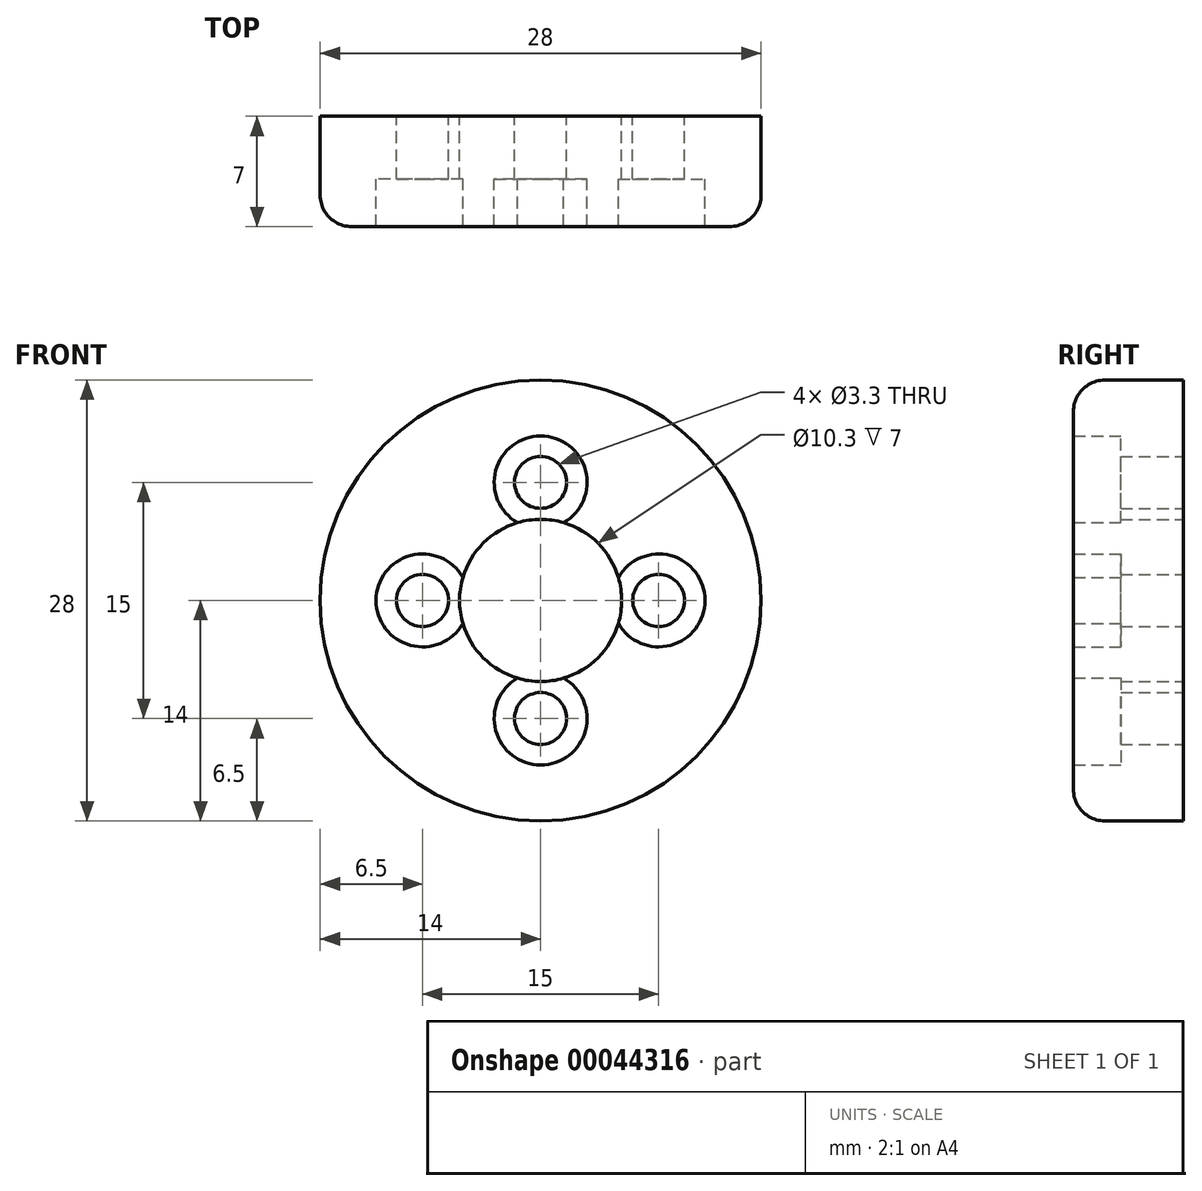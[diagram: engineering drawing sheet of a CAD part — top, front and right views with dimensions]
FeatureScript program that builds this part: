
annotation { "Feature Type Name" : "Feature", "Feature Type Description" : "" }
export const myFeature = defineFeature(function(context is Context, id is Id, definition is map)
    precondition{}
    {
        {
            var Q0;
            Q0=qCreatedBy(makeId("Front.planeOp"),FACE);
            var sketch = newSketch(context, id + "F0", { "sketchPlane" : qUnion([Q0])});
            skCircle(sketch, "E0", {"center": v(0, 0) * mm, "radius": 14 * mm});
            skCircle(sketch, "E1", {"center": v(0, 0) * mm, "radius": 5.15 * mm});
            skCircle(sketch, "E2", {"center": v(0, 0) * mm, "radius": 7.5 * mm, "construction": true});
            skLineSegment(sketch, "E3", {"start": v(0, 0) * mm, "end": v(0, 7.5) * mm});
            skCircle(sketch, "E4", {"center": v(0, 7.5) * mm, "radius": 1.65 * mm});
            skCircle(sketch, "E5.1.0", {"center": v(-7.5, 0) * mm, "radius": 1.65 * mm});
            skCircle(sketch, "E5.2.0", {"center": v(0, -7.5) * mm, "radius": 1.65 * mm});
            skCircle(sketch, "E5.3.0", {"center": v(7.5, 0) * mm, "radius": 1.65 * mm});
            skCircle(sketch, "E6", {"center": v(0, 7.5) * mm, "radius": 2.95 * mm});
            skCircle(sketch, "E7.1.0", {"center": v(-7.5, 0) * mm, "radius": 2.95 * mm});
            skCircle(sketch, "E7.2.0", {"center": v(0, -7.5) * mm, "radius": 2.95 * mm});
            skCircle(sketch, "E7.3.0", {"center": v(7.5, 0) * mm, "radius": 2.95 * mm});
            skSolve(sketch);
        }
        {
            var Q0;
            Q0=makeQuery(id+"F0.imprint","IMPRINT",FACE,{"disambiguationData":[TD([[makeQuery(id+"F0.imprint","IMPRINT",EDGE,{"derivedFrom":sQuery(id+"F0.wireOp",EDGE,"E0")}),1.0]])]});
            extrude(context, id + "F1", {"entities" : qUnion([Q0]), "depth" : 7 * mm});
        }
        {
            var Q0;
            Q0=makeQuery(id+"F0.imprint","IMPRINT",FACE,{"disambiguationData":[TD([[makeQuery(id+"F0.imprint","IMPRINT",EDGE,{"derivedFrom":sQuery(id+"F0.wireOp",EDGE,"E5.1.0")}),-1.0]])]});
            var Q1;
            Q1=makeQuery(id+"F0.imprint","IMPRINT",FACE,{"disambiguationData":[TD([[makeQuery(id+"F0.imprint","IMPRINT",EDGE,{"derivedFrom":sQuery(id+"F0.wireOp",EDGE,"E5.2.0")}),-1.0]])]});
            var Q2;
            Q2=makeQuery(id+"F0.imprint","IMPRINT",FACE,{"disambiguationData":[TD([[makeQuery(id+"F0.imprint","IMPRINT",EDGE,{"derivedFrom":sQuery(id+"F0.wireOp",EDGE,"E5.3.0")}),-1.0]])]});
            var Q3;
            Q3=makeQuery(id+"F0.imprint","IMPRINT",FACE,{"disambiguationData":[TD([[makeQuery(id+"F0.imprint","IMPRINT",EDGE,{"derivedFrom":sQuery(id+"F0.wireOp",EDGE,"E4")}),-1.0]])]});
            extrude(context, id + "F2", {"entities" : qUnion([Q0, Q1, Q2, Q3]), "operationType" : NewBodyOperationType.ADD, "depth" : 4 * mm});
        }
        {
            var Q0;
            Q0=makeQuery(id+"F0.imprint","IMPRINT",FACE,{"disambiguationData":[TD([[makeQuery(id+"F0.imprint","IMPRINT",EDGE,{"derivedFrom":sQuery(id+"F0.wireOp",EDGE,"E5.1.0")}),1.0]])]});
            var Q1;
            Q1=makeQuery(id+"F2.opExtrude","CAP_FACE",FACE,{"disambiguationData":[OSD([sQuery(id+"F0.wireOp",EDGE,"E1"),sQuery(id+"F0.wireOp",EDGE,"E5.1.0"),sQuery(id+"F0.wireOp",EDGE,"E7.1.0")])],"isStart":false});
            var Q2;
            Q2=makeQuery(id+"F0.imprint","IMPRINT",FACE,{"disambiguationData":[TD([[makeQuery(id+"F0.imprint","IMPRINT",EDGE,{"derivedFrom":sQuery(id+"F0.wireOp",EDGE,"E5.1.0")}),-1.0]])]});
            extrude(context, id + "F3", {"entities" : qUnion([Q0, Q1, Q2]), "depth" : 25 * mm});
        }
        {
            var Q0;
            Q0=makeQuery(id+"F3.opExtrude","SWEPT_BODY",BODY,{"disambiguationData":[OSD([sQuery(id+"F0.wireOp",EDGE,"E1"),sQuery(id+"F0.wireOp",EDGE,"E5.1.0"),sQuery(id+"F0.wireOp",EDGE,"E7.1.0")])]});
            var Q1;
            Q1=makeQuery(id+"F3.opExtrude","SWEPT_BODY",BODY,{"disambiguationData":[OSD([sQuery(id+"F0.wireOp",EDGE,"E1"),sQuery(id+"F0.wireOp",EDGE,"E7.1.0")])]});
            deleteBodies(context, id + "F4", {"entities" : qUnion([Q0, Q1])});
        }
        {
            var Q0;
            Q0=makeQuery(id+"F1.opExtrude","CAP_EDGE",EDGE,{"disambiguationData":[OSD([sQuery(id+"F0.wireOp",EDGE,"E0")])],"isStart":false});
            fillet(context, id + "F5", {"entities" : qUnion([Q0]), "radius" : 2 * mm, "tangentPropagation" : true, "allowEdgeOverflow" : false});
        }
    });
